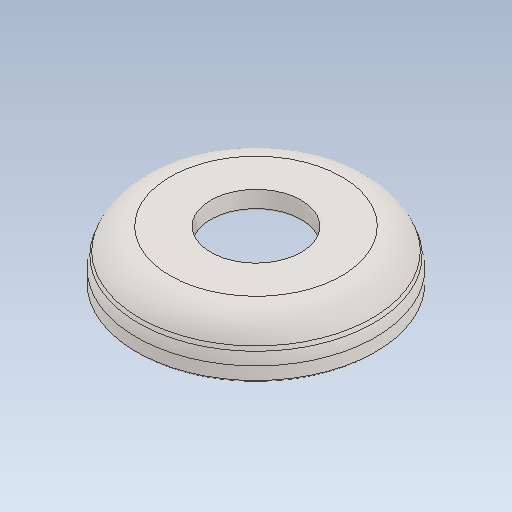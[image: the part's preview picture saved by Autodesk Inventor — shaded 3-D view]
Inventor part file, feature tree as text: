
AUTODESK INVENTOR PART (.ipt)
format: ipt  version: 2021 (Build 250183000, 183)  size: 166,400 bytes
history: mixed  units: in
note: dims shown in document units (in); Inventor stores cm internally (conversion verified against a paired STEP export)
features: revolve x1, imported_body x1
ambient origin geometry x8: Origin, YZ Plane, XZ Plane, XY Plane, X Axis, Y Axis, Z Axis, Center Point
bodies: Solid1 (imported_parasolid)
feature tree (2):
  revolve  "Revolve1"  [1 undecoded]
  imported_body  NMx_Import_Brep_tag  [imported B-rep: ~13 faces, bbox_mm=[0.0, 5.415495, 7.806974]]
note: 1 required parameter value undecoded (feature->parameter linkage not recoverable at this tier; creation-order binding heuristic only, values carry confidence <= 0.55)
